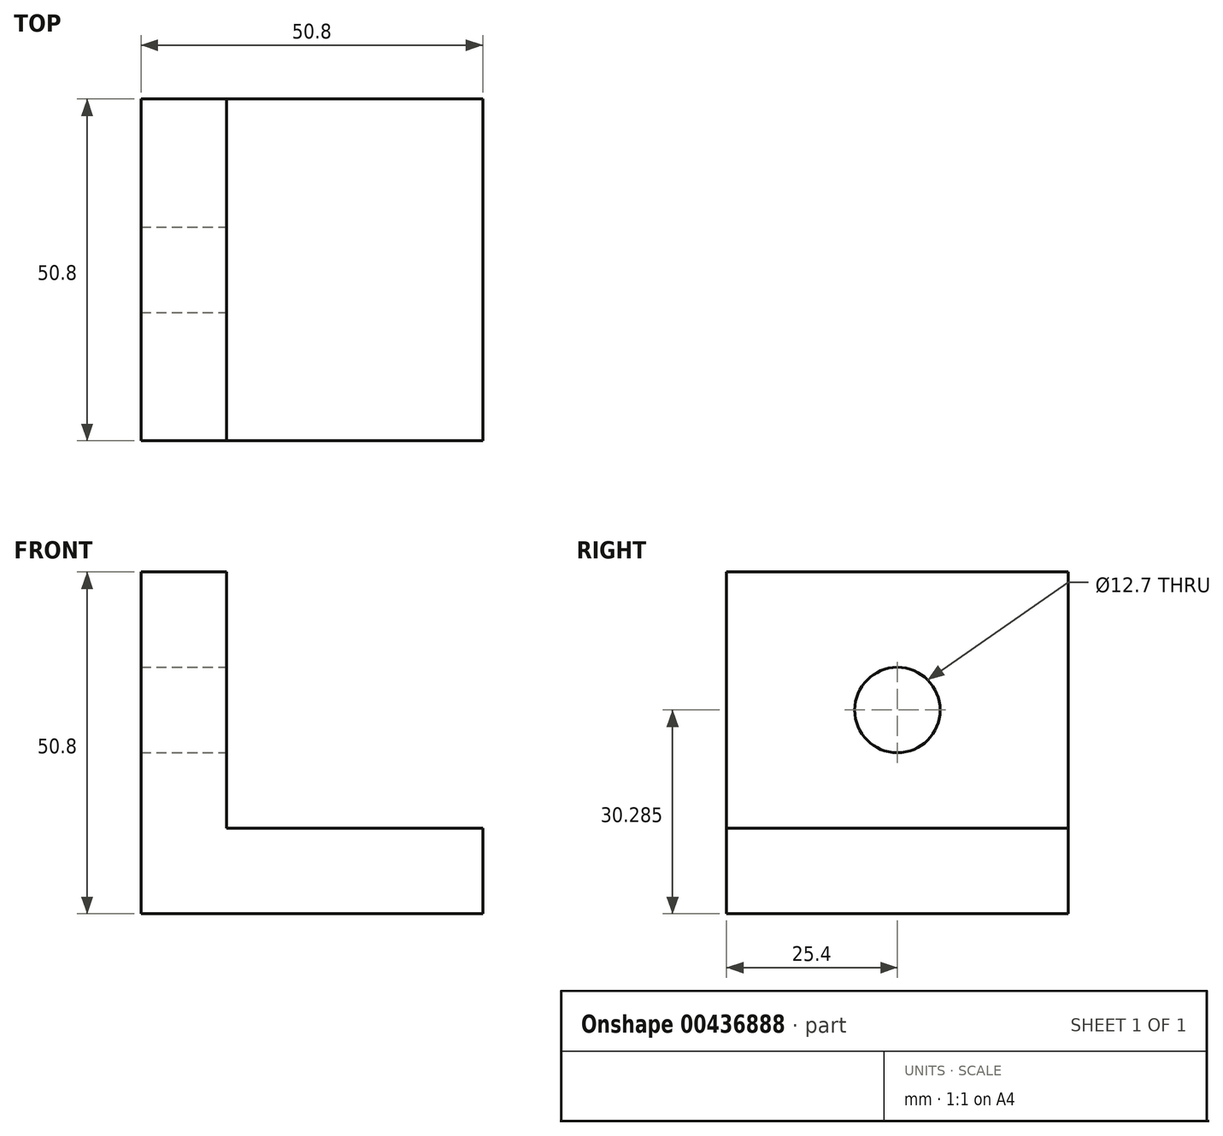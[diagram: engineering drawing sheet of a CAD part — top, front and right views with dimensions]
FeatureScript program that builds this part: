
annotation { "Feature Type Name" : "Feature", "Feature Type Description" : "" }
export const myFeature = defineFeature(function(context is Context, id is Id, definition is map)
    precondition{}
    {
        {
            var Q0;
            Q0=qCreatedBy(makeId("Front.planeOp"),FACE);
            var sketch = newSketch(context, id + "F0", { "sketchPlane" : qUnion([Q0])});
            skLineSegment(sketch, "E0", {"start": v(-74.19, 23.32) * mm, "end": v(-74.19, -27.48) * mm});
            skLineSegment(sketch, "E1", {"start": v(-74.19, -27.48) * mm, "end": v(-23.39, -27.48) * mm});
            skLineSegment(sketch, "E2", {"start": v(-23.39, -27.48) * mm, "end": v(-23.39, -14.78) * mm});
            skLineSegment(sketch, "E3", {"start": v(-23.39, -14.78) * mm, "end": v(-61.49, -14.78) * mm});
            skLineSegment(sketch, "E4", {"start": v(-61.49, -14.78) * mm, "end": v(-61.49, 23.32) * mm});
            skLineSegment(sketch, "E5", {"start": v(-61.49, 23.32) * mm, "end": v(-74.19, 23.32) * mm});
            skSolve(sketch);
        }
        {
            var Q0;
            Q0=makeQuery(id+"F0.imprint","IMPRINT",FACE,{"disambiguationData":[TD([[makeQuery(id+"F0.imprint","IMPRINT",EDGE,{"derivedFrom":sQuery(id+"F0.wireOp",EDGE,"E0")}),1.0]])]});
            extrude(context, id + "F1", {"entities" : qUnion([Q0]), "endBound" : BoundingType.SYMMETRIC, "depth" : 50.8 * mm});
        }
        {
            var Q0;
            Q0=makeQuery(id+"F1.opExtrude","SWEPT_FACE",FACE,{"disambiguationData":[OSD([sQuery(id+"F0.wireOp",EDGE,"E4")])]});
            var sketch = newSketch(context, id + "F2", { "sketchPlane" : qUnion([Q0])});
            skCircle(sketch, "E6", {"center": v(0, 2.8) * mm, "radius": 6.35 * mm});
            skSolve(sketch);
        }
        {
            var Q0;
            Q0=makeQuery(id+"F2.imprint","IMPRINT",FACE,{"disambiguationData":[TD([[makeQuery(id+"F2.imprint","IMPRINT",EDGE,{"derivedFrom":sQuery(id+"F2.wireOp",EDGE,"E6")}),1.0]])]});
            extrude(context, id + "F3", {"entities" : qUnion([Q0]), "operationType" : NewBodyOperationType.REMOVE, "endBound" : BoundingType.THROUGH_ALL, "oppositeDirection" : true, "depth" : 25.4 * mm});
        }
    });
